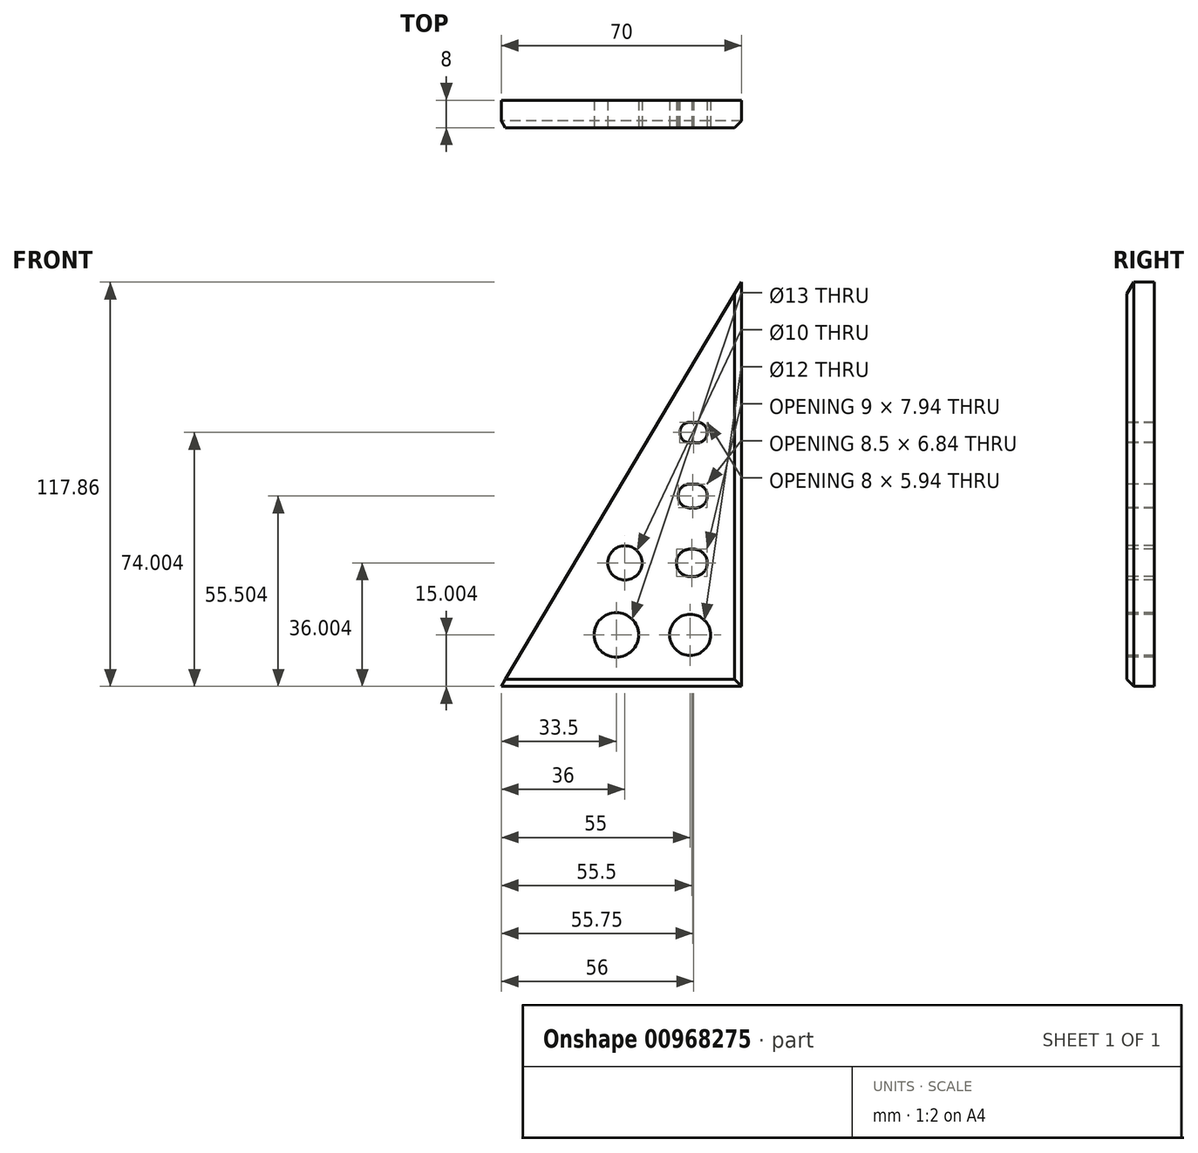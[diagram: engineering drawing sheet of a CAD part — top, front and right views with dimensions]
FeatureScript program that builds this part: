
annotation { "Feature Type Name" : "Feature", "Feature Type Description" : "" }
export const myFeature = defineFeature(function(context is Context, id is Id, definition is map)
    precondition{}
    {
        {
            var Q0;
            Q0=qCreatedBy(makeId("Front.planeOp"),FACE);
            var sketch = newSketch(context, id + "F0", { "sketchPlane" : qUnion([Q0])});
            skLineSegment(sketch, "E0", {"start": v(0, -74.8) * mm, "end": v(0, 65.2) * mm});
            skLineSegment(sketch, "E1", {"start": v(0, -74.8) * mm, "end": v(-70, -74.8) * mm});
            skLineSegment(sketch, "E2", {"start": v(-70, -74.8) * mm, "end": v(0, 65.2) * mm});
            skSolve(sketch);
        }
        {
            var Q0;
            Q0=makeQuery(id+"F0.imprint","IMPRINT",FACE,{"disambiguationData":[TD([[makeQuery(id+"F0.imprint","IMPRINT",EDGE,{"derivedFrom":sQuery(id+"F0.wireOp",EDGE,"E0")}),1.0]])]});
            extrude(context, id + "F1", {"entities" : qUnion([Q0]), "depth" : 8 * mm, "offsetDistance" : 25 * mm});
        }
        {
            var Q0;
            Q0=makeQuery(id+"F1.opExtrude","CAP_FACE",FACE,{"disambiguationData":[OSD([sQuery(id+"F0.wireOp",EDGE,"E0"),sQuery(id+"F0.wireOp",EDGE,"E1"),sQuery(id+"F0.wireOp",EDGE,"E2")])],"isStart":false});
            var sketch = newSketch(context, id + "F2", { "sketchPlane" : qUnion([Q0])});
            skLineSegment(sketch, "E3", {"start": v(0, -74.8) * mm, "end": v(-15, -74.8) * mm});
            skLineSegment(sketch, "E4", {"start": v(-15, -74.8) * mm, "end": v(-15, -64.8) * mm});
            skLineSegment(sketch, "E5", {"start": v(-15, -64.8) * mm, "end": v(-15, -58.3) * mm});
            skCircle(sketch, "E6", {"center": v(-15, -58.3) * mm, "radius": 6.5 * mm});
            skLineSegment(sketch, "E7", {"start": v(-15, -58.3) * mm, "end": v(-15, -33.8) * mm});
            skCircle(sketch, "E8", {"center": v(-15, -33.8) * mm, "radius": 6 * mm});
            skLineSegment(sketch, "E9", {"start": v(-15, -33.8) * mm, "end": v(-15, -10.8) * mm});
            skCircle(sketch, "E10", {"center": v(-15, -10.8) * mm, "radius": 5 * mm});
            skLineSegment(sketch, "E11", {"start": v(-15, -10.8) * mm, "end": v(-15, 10.2) * mm});
            skCircle(sketch, "E12", {"center": v(-15, 10.2) * mm, "radius": 4 * mm});
            skLineSegment(sketch, "E13", {"start": v(0, 65.2) * mm, "end": v(0, 115.2) * mm});
            skLineSegment(sketch, "E14", {"start": v(0, 115.2) * mm, "end": v(-70, -74.8) * mm});
            skSolve(sketch);
        }
        {
            var Q0;
            Q0=makeQuery(id+"F2.imprint","IMPRINT",FACE,{"disambiguationData":[TD([[makeQuery(id+"F2.imprint","IMPRINT",EDGE,{"derivedFrom":sQuery(id+"F2.wireOp",EDGE,"E13")}),1.0]])]});
            extrude(context, id + "F3", {"entities" : qUnion([Q0]), "operationType" : NewBodyOperationType.ADD, "oppositeDirection" : true, "depth" : 8 * mm, "offsetDistance" : 25 * mm});
        }
        {
            var Q0;
            {var subQ0=sQuery(id+"F0.wireOp",EDGE,"E2");Q0=makeQuery(id+"F3.boolean.opBoolean","MERGE",FACE,{"derivedFrom":[makeQuery(id+"F1.opExtrude","CAP_FACE",FACE,{"disambiguationData":[OSD([sQuery(id+"F0.wireOp",EDGE,"E0"),sQuery(id+"F0.wireOp",EDGE,"E1"),subQ0])],"isStart":false}),makeQuery(id+"F3.opExtrude","CAP_FACE",FACE,{"disambiguationData":[OSD([subQ0,sQuery(id+"F2.wireOp",EDGE,"E13"),sQuery(id+"F2.wireOp",EDGE,"E14")])],"isStart":true})]});}
            var sketch = newSketch(context, id + "F4", { "sketchPlane" : qUnion([Q0])});
            skLineSegment(sketch, "E15", {"start": v(0, 115.2) * mm, "end": v(0, 65.2) * mm});
            skLineSegment(sketch, "E16", {"start": v(0, 65.2) * mm, "end": v(-70, -74.8) * mm});
            skLineSegment(sketch, "E17", {"start": v(-70, -74.8) * mm, "end": v(0, 115.2) * mm});
            skSolve(sketch);
        }
        {
            var Q0;
            Q0=makeQuery(id+"F4.imprint","IMPRINT",FACE,{"disambiguationData":[TD([[makeQuery(id+"F4.imprint","IMPRINT",EDGE,{"derivedFrom":sQuery(id+"F4.wireOp",EDGE,"E15")}),1.0]])]});
            extrude(context, id + "F5", {"entities" : qUnion([Q0]), "operationType" : NewBodyOperationType.REMOVE, "oppositeDirection" : true, "depth" : 25 * mm, "offsetDistance" : 25 * mm});
        }
        {
            var Q0;
            {var subQ0=sQuery(id+"F0.wireOp",EDGE,"E2");Q0=makeQuery(id+"F3.boolean.opBoolean","MERGE",FACE,{"derivedFrom":[makeQuery(id+"F1.opExtrude","CAP_FACE",FACE,{"disambiguationData":[OSD([sQuery(id+"F0.wireOp",EDGE,"E0"),sQuery(id+"F0.wireOp",EDGE,"E1"),subQ0])],"isStart":false}),makeQuery(id+"F3.opExtrude","CAP_FACE",FACE,{"disambiguationData":[OSD([subQ0,sQuery(id+"F2.wireOp",EDGE,"E13"),sQuery(id+"F2.wireOp",EDGE,"E14")])],"isStart":true})]});}
            var sketch = newSketch(context, id + "F6", { "sketchPlane" : qUnion([Q0])});
            skLineSegment(sketch, "E18", {"start": v(0, -74.8) * mm, "end": v(-10, -74.8) * mm});
            skLineSegment(sketch, "E19", {"start": v(-10, -74.8) * mm, "end": v(-10, -64.8) * mm});
            skLineSegment(sketch, "E20", {"start": v(-10, -64.8) * mm, "end": v(-10, -59.8) * mm});
            skCircle(sketch, "E21", {"center": v(-10, -59.8) * mm, "radius": 5 * mm});
            skLineSegment(sketch, "E22", {"start": v(-10, -59.8) * mm, "end": v(-10, -38.8) * mm});
            skCircle(sketch, "E23", {"center": v(-10, -38.8) * mm, "radius": 4 * mm});
            skLineSegment(sketch, "E24", {"start": v(-10, -38.8) * mm, "end": v(-10, -19.3) * mm});
            skCircle(sketch, "E25", {"center": v(-10, -19.3) * mm, "radius": 3.5 * mm});
            skLineSegment(sketch, "E26", {"start": v(-10, -19.3) * mm, "end": v(-10, -0.8) * mm});
            skCircle(sketch, "E27", {"center": v(-10, -0.8) * mm, "radius": 3 * mm});
            skSolve(sketch);
        }
        {
            var Q0;
            {var subQ0=sQuery(id+"F6.wireOp",EDGE,"E20");Q0=makeQuery(id+"F6.imprint","IMPRINT",FACE,{"disambiguationData":[TD([[makeQuery(id+"F6.imprint","IMPRINT",EDGE,{"derivedFrom":subQ0}),-1.0]])]});}
            var Q1;
            {var subQ0=sQuery(id+"F6.wireOp",EDGE,"E20");Q1=makeQuery(id+"F6.imprint","IMPRINT",FACE,{"disambiguationData":[TD([[makeQuery(id+"F6.imprint","IMPRINT",EDGE,{"derivedFrom":subQ0}),1.0]])]});}
            var Q2;
            {var subQ0=sQuery(id+"F6.wireOp",EDGE,"E24");var subQ1=sQuery(id+"F6.wireOp",EDGE,"E22");var subQ2=makeQuery(id+"F6.imprint","INTERSECT",VERTEX,{"derivedFrom":[subQ1,subQ0]});Q2=makeQuery(id+"F6.imprint","IMPRINT",FACE,{"disambiguationData":[TD([[makeQuery(id+"F6.imprint","IMPRINT",EDGE,{"disambiguationData":[TD([[subQ2,1.0]])],"derivedFrom":subQ1}),-1.0]])]});}
            var Q3;
            {var subQ0=sQuery(id+"F6.wireOp",EDGE,"E24");var subQ1=sQuery(id+"F6.wireOp",EDGE,"E22");var subQ2=makeQuery(id+"F6.imprint","INTERSECT",VERTEX,{"derivedFrom":[subQ1,subQ0]});Q3=makeQuery(id+"F6.imprint","IMPRINT",FACE,{"disambiguationData":[TD([[makeQuery(id+"F6.imprint","IMPRINT",EDGE,{"disambiguationData":[TD([[subQ2,1.0]])],"derivedFrom":subQ1}),1.0]])]});}
            var Q4;
            {var subQ0=sQuery(id+"F6.wireOp",EDGE,"E26");var subQ1=sQuery(id+"F6.wireOp",EDGE,"E24");var subQ2=makeQuery(id+"F6.imprint","INTERSECT",VERTEX,{"derivedFrom":[subQ1,subQ0]});Q4=makeQuery(id+"F6.imprint","IMPRINT",FACE,{"disambiguationData":[TD([[makeQuery(id+"F6.imprint","IMPRINT",EDGE,{"disambiguationData":[TD([[subQ2,1.0]])],"derivedFrom":subQ1}),-1.0]])]});}
            var Q5;
            {var subQ0=sQuery(id+"F6.wireOp",EDGE,"E26");var subQ1=sQuery(id+"F6.wireOp",EDGE,"E24");var subQ2=makeQuery(id+"F6.imprint","INTERSECT",VERTEX,{"derivedFrom":[subQ1,subQ0]});Q5=makeQuery(id+"F6.imprint","IMPRINT",FACE,{"disambiguationData":[TD([[makeQuery(id+"F6.imprint","IMPRINT",EDGE,{"disambiguationData":[TD([[subQ2,1.0]])],"derivedFrom":subQ1}),1.0]])]});}
            var Q6;
            Q6=makeQuery(id+"F6.imprint","IMPRINT",FACE,{"disambiguationData":[TD([[makeQuery(id+"F6.imprint","IMPRINT",EDGE,{"derivedFrom":sQuery(id+"F6.wireOp",EDGE,"E27")}),1.0]])]});
            extrude(context, id + "F7", {"entities" : qUnion([Q0, Q1, Q2, Q3, Q4, Q5, Q6]), "operationType" : NewBodyOperationType.REMOVE, "oppositeDirection" : true, "depth" : 25 * mm, "offsetDistance" : 25 * mm});
        }
        {
            var Q0;
            {var subQ0=sQuery(id+"F0.wireOp",EDGE,"E2");Q0=makeQuery(id+"F3.boolean.opBoolean","MERGE",FACE,{"derivedFrom":[makeQuery(id+"F1.opExtrude","CAP_FACE",FACE,{"disambiguationData":[OSD([sQuery(id+"F0.wireOp",EDGE,"E0"),sQuery(id+"F0.wireOp",EDGE,"E1"),subQ0])],"isStart":false}),makeQuery(id+"F3.opExtrude","CAP_FACE",FACE,{"disambiguationData":[OSD([subQ0,sQuery(id+"F2.wireOp",EDGE,"E13"),sQuery(id+"F2.wireOp",EDGE,"E14")])],"isStart":true})]});}
            var sketch = newSketch(context, id + "F8", { "sketchPlane" : qUnion([Q0])});
            skLineSegment(sketch, "E28", {"start": v(0, 65.2) * mm, "end": v(0, 35.2) * mm});
            skLineSegment(sketch, "E29", {"start": v(0, 35.2) * mm, "end": v(-70, -74.8) * mm});
            skLineSegment(sketch, "E30", {"start": v(-70, -74.8) * mm, "end": v(0, 65.2) * mm});
            skSolve(sketch);
        }
        {
            var Q0;
            Q0=makeQuery(id+"F8.imprint","IMPRINT",FACE,{"disambiguationData":[TD([[makeQuery(id+"F8.imprint","IMPRINT",EDGE,{"derivedFrom":sQuery(id+"F8.wireOp",EDGE,"E28")}),1.0]])]});
            extrude(context, id + "F9", {"entities" : qUnion([Q0]), "operationType" : NewBodyOperationType.REMOVE, "oppositeDirection" : true, "depth" : 25 * mm, "offsetDistance" : 25 * mm});
        }
        {
            var Q0;
            {var subQ0=sQuery(id+"F0.wireOp",EDGE,"E2");Q0=makeQuery(id+"F3.boolean.opBoolean","MERGE",FACE,{"derivedFrom":[makeQuery(id+"F1.opExtrude","CAP_FACE",FACE,{"disambiguationData":[OSD([sQuery(id+"F0.wireOp",EDGE,"E0"),sQuery(id+"F0.wireOp",EDGE,"E1"),subQ0])],"isStart":false}),makeQuery(id+"F3.opExtrude","CAP_FACE",FACE,{"disambiguationData":[OSD([subQ0,sQuery(id+"F2.wireOp",EDGE,"E13"),sQuery(id+"F2.wireOp",EDGE,"E14")])],"isStart":true})]});}
            var sketch = newSketch(context, id + "F10", { "sketchPlane" : qUnion([Q0])});
            skLineSegment(sketch, "E31", {"start": v(0, 35.2) * mm, "end": v(8.94, 49.24) * mm});
            skLineSegment(sketch, "E32", {"start": v(0, -74.8) * mm, "end": v(5, -74.8) * mm});
            skLineSegment(sketch, "E33", {"start": v(5, -74.8) * mm, "end": v(5, 43.05) * mm});
            skSolve(sketch);
        }
        {
            var Q0;
            Q0=makeQuery(id+"F10.imprint","IMPRINT",FACE,{"disambiguationData":[TD([[makeQuery(id+"F10.imprint","IMPRINT",EDGE,{"derivedFrom":sQuery(id+"F10.wireOp",EDGE,"E32")}),1.0]])]});
            extrude(context, id + "F11", {"entities" : qUnion([Q0]), "operationType" : NewBodyOperationType.ADD, "oppositeDirection" : true, "depth" : 8 * mm, "offsetDistance" : 25 * mm});
        }
        {
            var Q0;
            {var subQ0=sQuery(id+"F2.wireOp",EDGE,"E13");var subQ1=sQuery(id+"F0.wireOp",EDGE,"E0");var subQ2=sQuery(id+"F0.wireOp",EDGE,"E2");Q0=makeQuery(id+"F11.boolean.opBoolean","MERGE",FACE,{"derivedFrom":[makeQuery(id+"F3.boolean.opBoolean","MERGE",FACE,{"derivedFrom":[makeQuery(id+"F1.opExtrude","CAP_FACE",FACE,{"disambiguationData":[OSD([subQ1,sQuery(id+"F0.wireOp",EDGE,"E1"),subQ2])],"isStart":false}),makeQuery(id+"F3.opExtrude","CAP_FACE",FACE,{"disambiguationData":[OSD([subQ2,subQ0,sQuery(id+"F2.wireOp",EDGE,"E14")])],"isStart":true})]}),makeQuery(id+"F11.opExtrude","CAP_FACE",FACE,{"disambiguationData":[OSD([subQ1,subQ0,sQuery(id+"F10.wireOp",EDGE,"E31"),sQuery(id+"F10.wireOp",EDGE,"E32"),sQuery(id+"F10.wireOp",EDGE,"E33")])],"isStart":true})]});}
            var sketch = newSketch(context, id + "F12", { "sketchPlane" : qUnion([Q0])});
            skLineSegment(sketch, "E34", {"start": v(-70, -74.8) * mm, "end": v(-65, -74.8) * mm});
            skLineSegment(sketch, "E35", {"start": v(-65, -74.8) * mm, "end": v(5, 43.05) * mm});
            skLineSegment(sketch, "E36", {"start": v(5, 43.05) * mm, "end": v(-70, -74.8) * mm});
            skSolve(sketch);
        }
        {
            var Q0;
            Q0=makeQuery(id+"F12.imprint","IMPRINT",FACE,{"disambiguationData":[TD([[makeQuery(id+"F12.imprint","IMPRINT",EDGE,{"derivedFrom":sQuery(id+"F12.wireOp",EDGE,"E34")}),-1.0]])]});
            extrude(context, id + "F13", {"entities" : qUnion([Q0]), "operationType" : NewBodyOperationType.REMOVE, "oppositeDirection" : true, "depth" : 25 * mm, "offsetDistance" : 25 * mm});
        }
        {
            var Q0;
            {var subQ0=sQuery(id+"F2.wireOp",EDGE,"E13");var subQ1=sQuery(id+"F0.wireOp",EDGE,"E0");var subQ2=sQuery(id+"F0.wireOp",EDGE,"E2");Q0=makeQuery(id+"F11.boolean.opBoolean","MERGE",FACE,{"derivedFrom":[makeQuery(id+"F3.boolean.opBoolean","MERGE",FACE,{"derivedFrom":[makeQuery(id+"F1.opExtrude","CAP_FACE",FACE,{"disambiguationData":[OSD([subQ1,sQuery(id+"F0.wireOp",EDGE,"E1"),subQ2])],"isStart":false}),makeQuery(id+"F3.opExtrude","CAP_FACE",FACE,{"disambiguationData":[OSD([subQ2,subQ0,sQuery(id+"F2.wireOp",EDGE,"E14")])],"isStart":true})]}),makeQuery(id+"F11.opExtrude","CAP_FACE",FACE,{"disambiguationData":[OSD([subQ1,subQ0,sQuery(id+"F10.wireOp",EDGE,"E31"),sQuery(id+"F10.wireOp",EDGE,"E32"),sQuery(id+"F10.wireOp",EDGE,"E33")])],"isStart":true})]});}
            var sketch = newSketch(context, id + "F14", { "sketchPlane" : qUnion([Q0])});
            skCircle(sketch, "E37", {"center": v(-10, -38.8) * mm, "radius": 6.34 * mm});
            skCircle(sketch, "E38", {"center": v(-10, -19.3) * mm, "radius": 6.83 * mm});
            skCircle(sketch, "E39", {"center": v(-10, -0.8) * mm, "radius": 5.3 * mm});
            skSolve(sketch);
        }
        {
            var Q0;
            Q0=makeQuery(id+"F14.imprint","IMPRINT",FACE,{"disambiguationData":[TD([[makeQuery(id+"F14.imprint","IMPRINT",EDGE,{"derivedFrom":sQuery(id+"F14.wireOp",EDGE,"E37")}),1.0]])]});
            var Q1;
            Q1=makeQuery(id+"F14.imprint","IMPRINT",FACE,{"disambiguationData":[TD([[makeQuery(id+"F14.imprint","IMPRINT",EDGE,{"derivedFrom":makeQuery(id+"F7.boolean.opBoolean","COPY",EDGE,{"derivedFrom":makeQuery(id+"F7.opExtrude","CAP_EDGE",EDGE,{"disambiguationData":[OSD([sQuery(id+"F6.wireOp",EDGE,"E23")])],"isStart":true})})}),1.0]])]});
            var Q2;
            Q2=makeQuery(id+"F14.imprint","IMPRINT",FACE,{"disambiguationData":[TD([[makeQuery(id+"F14.imprint","IMPRINT",EDGE,{"derivedFrom":sQuery(id+"F14.wireOp",EDGE,"E38")}),1.0]])]});
            var Q3;
            Q3=makeQuery(id+"F14.imprint","IMPRINT",FACE,{"disambiguationData":[TD([[makeQuery(id+"F14.imprint","IMPRINT",EDGE,{"derivedFrom":makeQuery(id+"F7.boolean.opBoolean","COPY",EDGE,{"derivedFrom":makeQuery(id+"F7.opExtrude","CAP_EDGE",EDGE,{"disambiguationData":[OSD([sQuery(id+"F6.wireOp",EDGE,"E25")])],"isStart":true})})}),1.0]])]});
            var Q4;
            Q4=makeQuery(id+"F14.imprint","IMPRINT",FACE,{"disambiguationData":[TD([[makeQuery(id+"F14.imprint","IMPRINT",EDGE,{"derivedFrom":sQuery(id+"F14.wireOp",EDGE,"E39")}),1.0]])]});
            var Q5;
            Q5=makeQuery(id+"F14.imprint","IMPRINT",FACE,{"disambiguationData":[TD([[makeQuery(id+"F14.imprint","IMPRINT",EDGE,{"derivedFrom":makeQuery(id+"F7.boolean.opBoolean","COPY",EDGE,{"derivedFrom":makeQuery(id+"F7.opExtrude","CAP_EDGE",EDGE,{"disambiguationData":[OSD([sQuery(id+"F6.wireOp",EDGE,"E27")])],"isStart":true})})}),1.0]])]});
            extrude(context, id + "F15", {"entities" : qUnion([Q0, Q1, Q2, Q3, Q4, Q5]), "operationType" : NewBodyOperationType.ADD, "oppositeDirection" : true, "depth" : 8 * mm, "offsetDistance" : 25 * mm});
        }
        {
            var Q0;
            {var subQ0=sQuery(id+"F2.wireOp",EDGE,"E13");var subQ1=sQuery(id+"F0.wireOp",EDGE,"E0");var subQ2=sQuery(id+"F0.wireOp",EDGE,"E2");Q0=makeQuery(id+"F15.boolean.opBoolean","MERGE",FACE,{"derivedFrom":[makeQuery(id+"F11.boolean.opBoolean","MERGE",FACE,{"derivedFrom":[makeQuery(id+"F3.boolean.opBoolean","MERGE",FACE,{"derivedFrom":[makeQuery(id+"F1.opExtrude","CAP_FACE",FACE,{"disambiguationData":[OSD([subQ1,sQuery(id+"F0.wireOp",EDGE,"E1"),subQ2])],"isStart":false}),makeQuery(id+"F3.opExtrude","CAP_FACE",FACE,{"disambiguationData":[OSD([subQ2,subQ0,sQuery(id+"F2.wireOp",EDGE,"E14")])],"isStart":true})]}),makeQuery(id+"F11.opExtrude","CAP_FACE",FACE,{"disambiguationData":[OSD([subQ1,subQ0,sQuery(id+"F10.wireOp",EDGE,"E31"),sQuery(id+"F10.wireOp",EDGE,"E32"),sQuery(id+"F10.wireOp",EDGE,"E33")])],"isStart":true})]}),makeQuery(id+"F15.opExtrude","CAP_FACE",FACE,{"disambiguationData":[OSD([sQuery(id+"F14.wireOp",EDGE,"E37")])],"isStart":true}),makeQuery(id+"F15.opExtrude","CAP_FACE",FACE,{"disambiguationData":[OSD([sQuery(id+"F14.wireOp",EDGE,"E38")])],"isStart":true}),makeQuery(id+"F15.opExtrude","CAP_FACE",FACE,{"disambiguationData":[OSD([sQuery(id+"F14.wireOp",EDGE,"E39")])],"isStart":true})]});}
            var sketch = newSketch(context, id + "F16", { "sketchPlane" : qUnion([Q0])});
            skLineSegment(sketch, "E40", {"start": v(-10, -59.8) * mm, "end": v(-5, -59.8) * mm});
            skLineSegment(sketch, "E41", {"start": v(-5, -59.8) * mm, "end": v(-5, 40.97) * mm});
            skLineSegment(sketch, "E42", {"start": v(-5, -59.8) * mm, "end": v(-5, -38.8) * mm});
            skLineSegment(sketch, "E43", {"start": v(-5, -38.8) * mm, "end": v(-9, -38.8) * mm});
            skCircle(sketch, "E44", {"center": v(-9, -38.8) * mm, "radius": 4 * mm});
            skLineSegment(sketch, "E45", {"start": v(-5, -38.8) * mm, "end": v(-5, -19.3) * mm});
            skLineSegment(sketch, "E46", {"start": v(-5, -19.3) * mm, "end": v(-8.5, -19.3) * mm});
            skCircle(sketch, "E47", {"center": v(-8.5, -19.3) * mm, "radius": 3.5 * mm});
            skLineSegment(sketch, "E48", {"start": v(-5, -19.3) * mm, "end": v(-5, -0.8) * mm});
            skLineSegment(sketch, "E49", {"start": v(-5, -0.8) * mm, "end": v(-8, -0.8) * mm});
            skCircle(sketch, "E50", {"center": v(-8, -0.8) * mm, "radius": 3 * mm});
            skSolve(sketch);
        }
        {
            var Q0;
            Q0=makeQuery(id+"F16.imprint","IMPRINT",FACE,{"disambiguationData":[TD([[makeQuery(id+"F16.imprint","IMPRINT",EDGE,{"derivedFrom":sQuery(id+"F16.wireOp",EDGE,"E44")}),1.0]])]});
            var Q1;
            Q1=makeQuery(id+"F16.imprint","IMPRINT",FACE,{"disambiguationData":[TD([[makeQuery(id+"F16.imprint","IMPRINT",EDGE,{"derivedFrom":sQuery(id+"F16.wireOp",EDGE,"E47")}),1.0]])]});
            var Q2;
            Q2=makeQuery(id+"F16.imprint","IMPRINT",FACE,{"disambiguationData":[TD([[makeQuery(id+"F16.imprint","IMPRINT",EDGE,{"derivedFrom":sQuery(id+"F16.wireOp",EDGE,"E50")}),1.0]])]});
            extrude(context, id + "F17", {"entities" : qUnion([Q0, Q1, Q2]), "operationType" : NewBodyOperationType.REMOVE, "oppositeDirection" : true, "depth" : 25 * mm, "offsetDistance" : 25 * mm});
        }
        {
            var Q0;
            {var subQ0=sQuery(id+"F2.wireOp",EDGE,"E13");var subQ1=sQuery(id+"F0.wireOp",EDGE,"E0");var subQ2=sQuery(id+"F0.wireOp",EDGE,"E2");Q0=makeQuery(id+"F15.boolean.opBoolean","MERGE",FACE,{"derivedFrom":[makeQuery(id+"F11.boolean.opBoolean","MERGE",FACE,{"derivedFrom":[makeQuery(id+"F3.boolean.opBoolean","MERGE",FACE,{"derivedFrom":[makeQuery(id+"F1.opExtrude","CAP_FACE",FACE,{"disambiguationData":[OSD([subQ1,sQuery(id+"F0.wireOp",EDGE,"E1"),subQ2])],"isStart":false}),makeQuery(id+"F3.opExtrude","CAP_FACE",FACE,{"disambiguationData":[OSD([subQ2,subQ0,sQuery(id+"F2.wireOp",EDGE,"E14")])],"isStart":true})]}),makeQuery(id+"F11.opExtrude","CAP_FACE",FACE,{"disambiguationData":[OSD([subQ1,subQ0,sQuery(id+"F10.wireOp",EDGE,"E31"),sQuery(id+"F10.wireOp",EDGE,"E32"),sQuery(id+"F10.wireOp",EDGE,"E33")])],"isStart":true})]}),makeQuery(id+"F15.opExtrude","CAP_FACE",FACE,{"disambiguationData":[OSD([sQuery(id+"F14.wireOp",EDGE,"E37")])],"isStart":true}),makeQuery(id+"F15.opExtrude","CAP_FACE",FACE,{"disambiguationData":[OSD([sQuery(id+"F14.wireOp",EDGE,"E38")])],"isStart":true}),makeQuery(id+"F15.opExtrude","CAP_FACE",FACE,{"disambiguationData":[OSD([sQuery(id+"F14.wireOp",EDGE,"E39")])],"isStart":true})]});}
            var sketch = newSketch(context, id + "F18", { "sketchPlane" : qUnion([Q0])});
            skLineSegment(sketch, "E51", {"start": v(-10, -59.8) * mm, "end": v(-31.5, -59.8) * mm});
            skCircle(sketch, "E52", {"center": v(-31.5, -59.8) * mm, "radius": 6.5 * mm});
            skLineSegment(sketch, "E53", {"start": v(-9, -38.8) * mm, "end": v(-29, -38.8) * mm});
            skCircle(sketch, "E54", {"center": v(-29, -38.8) * mm, "radius": 6 * mm});
            skSolve(sketch);
        }
        {
            var Q0;
            Q0=makeQuery(id+"F18.imprint","IMPRINT",FACE,{"disambiguationData":[TD([[makeQuery(id+"F18.imprint","IMPRINT",EDGE,{"derivedFrom":sQuery(id+"F18.wireOp",EDGE,"E52")}),1.0]])]});
            var Q1;
            Q1=makeQuery(id+"F18.imprint","IMPRINT",FACE,{"disambiguationData":[TD([[makeQuery(id+"F18.imprint","IMPRINT",EDGE,{"derivedFrom":sQuery(id+"F18.wireOp",EDGE,"E54")}),1.0]])]});
            extrude(context, id + "F19", {"entities" : qUnion([Q0, Q1]), "operationType" : NewBodyOperationType.REMOVE, "oppositeDirection" : true, "depth" : 25 * mm, "offsetDistance" : 25 * mm});
        }
        {
            var Q0;
            {var subQ0=sQuery(id+"F2.wireOp",EDGE,"E13");var subQ1=sQuery(id+"F0.wireOp",EDGE,"E0");var subQ2=sQuery(id+"F0.wireOp",EDGE,"E2");Q0=makeQuery(id+"F15.boolean.opBoolean","MERGE",FACE,{"derivedFrom":[makeQuery(id+"F11.boolean.opBoolean","MERGE",FACE,{"derivedFrom":[makeQuery(id+"F3.boolean.opBoolean","MERGE",FACE,{"derivedFrom":[makeQuery(id+"F1.opExtrude","CAP_FACE",FACE,{"disambiguationData":[OSD([subQ1,sQuery(id+"F0.wireOp",EDGE,"E1"),subQ2])],"isStart":false}),makeQuery(id+"F3.opExtrude","CAP_FACE",FACE,{"disambiguationData":[OSD([subQ2,subQ0,sQuery(id+"F2.wireOp",EDGE,"E14")])],"isStart":true})]}),makeQuery(id+"F11.opExtrude","CAP_FACE",FACE,{"disambiguationData":[OSD([subQ1,subQ0,sQuery(id+"F10.wireOp",EDGE,"E31"),sQuery(id+"F10.wireOp",EDGE,"E32"),sQuery(id+"F10.wireOp",EDGE,"E33")])],"isStart":true})]}),makeQuery(id+"F15.opExtrude","CAP_FACE",FACE,{"disambiguationData":[OSD([sQuery(id+"F14.wireOp",EDGE,"E37")])],"isStart":true}),makeQuery(id+"F15.opExtrude","CAP_FACE",FACE,{"disambiguationData":[OSD([sQuery(id+"F14.wireOp",EDGE,"E38")])],"isStart":true}),makeQuery(id+"F15.opExtrude","CAP_FACE",FACE,{"disambiguationData":[OSD([sQuery(id+"F14.wireOp",EDGE,"E39")])],"isStart":true})]});}
            var sketch = newSketch(context, id + "F20", { "sketchPlane" : qUnion([Q0])});
            skCircle(sketch, "E55", {"center": v(-10, -59.8) * mm, "radius": 6.5 * mm});
            skSolve(sketch);
        }
        {
            var Q0;
            Q0=makeQuery(id+"F20.imprint","IMPRINT",FACE,{"disambiguationData":[TD([[makeQuery(id+"F20.imprint","IMPRINT",EDGE,{"derivedFrom":sQuery(id+"F20.wireOp",EDGE,"E55")}),1.0]])]});
            extrude(context, id + "F21", {"entities" : qUnion([Q0]), "operationType" : NewBodyOperationType.REMOVE, "oppositeDirection" : true, "depth" : 25 * mm, "offsetDistance" : 25 * mm});
        }
        {
            var Q0;
            {var subQ0=sQuery(id+"F2.wireOp",EDGE,"E13");var subQ1=sQuery(id+"F0.wireOp",EDGE,"E0");var subQ2=sQuery(id+"F0.wireOp",EDGE,"E2");Q0=makeQuery(id+"F15.boolean.opBoolean","MERGE",FACE,{"derivedFrom":[makeQuery(id+"F11.boolean.opBoolean","MERGE",FACE,{"derivedFrom":[makeQuery(id+"F3.boolean.opBoolean","MERGE",FACE,{"derivedFrom":[makeQuery(id+"F1.opExtrude","CAP_FACE",FACE,{"disambiguationData":[OSD([subQ1,sQuery(id+"F0.wireOp",EDGE,"E1"),subQ2])],"isStart":false}),makeQuery(id+"F3.opExtrude","CAP_FACE",FACE,{"disambiguationData":[OSD([subQ2,subQ0,sQuery(id+"F2.wireOp",EDGE,"E14")])],"isStart":true})]}),makeQuery(id+"F11.opExtrude","CAP_FACE",FACE,{"disambiguationData":[OSD([subQ1,subQ0,sQuery(id+"F10.wireOp",EDGE,"E31"),sQuery(id+"F10.wireOp",EDGE,"E32"),sQuery(id+"F10.wireOp",EDGE,"E33")])],"isStart":true})]}),makeQuery(id+"F15.opExtrude","CAP_FACE",FACE,{"disambiguationData":[OSD([sQuery(id+"F14.wireOp",EDGE,"E37")])],"isStart":true}),makeQuery(id+"F15.opExtrude","CAP_FACE",FACE,{"disambiguationData":[OSD([sQuery(id+"F14.wireOp",EDGE,"E38")])],"isStart":true}),makeQuery(id+"F15.opExtrude","CAP_FACE",FACE,{"disambiguationData":[OSD([sQuery(id+"F14.wireOp",EDGE,"E39")])],"isStart":true})]});}
            var sketch = newSketch(context, id + "F22", { "sketchPlane" : qUnion([Q0])});
            skCircle(sketch, "E56", {"center": v(-29, -38.8) * mm, "radius": 5 * mm});
            skSolve(sketch);
        }
        {
            var Q0;
            Q0=makeQuery(id+"F22.imprint","IMPRINT",FACE,{"disambiguationData":[TD([[makeQuery(id+"F22.imprint","IMPRINT",EDGE,{"derivedFrom":sQuery(id+"F22.wireOp",EDGE,"E56")}),-1.0]])]});
            extrude(context, id + "F23", {"entities" : qUnion([Q0]), "operationType" : NewBodyOperationType.ADD, "oppositeDirection" : true, "depth" : 8 * mm, "offsetDistance" : 25 * mm});
        }
        {
            var Q0;
            {var subQ0=sQuery(id+"F2.wireOp",EDGE,"E13");var subQ1=sQuery(id+"F0.wireOp",EDGE,"E0");var subQ2=sQuery(id+"F0.wireOp",EDGE,"E2");Q0=makeQuery(id+"F23.boolean.opBoolean","MERGE",FACE,{"derivedFrom":[makeQuery(id+"F15.boolean.opBoolean","MERGE",FACE,{"derivedFrom":[makeQuery(id+"F11.boolean.opBoolean","MERGE",FACE,{"derivedFrom":[makeQuery(id+"F3.boolean.opBoolean","MERGE",FACE,{"derivedFrom":[makeQuery(id+"F1.opExtrude","CAP_FACE",FACE,{"disambiguationData":[OSD([subQ1,sQuery(id+"F0.wireOp",EDGE,"E1"),subQ2])],"isStart":false}),makeQuery(id+"F3.opExtrude","CAP_FACE",FACE,{"disambiguationData":[OSD([subQ2,subQ0,sQuery(id+"F2.wireOp",EDGE,"E14")])],"isStart":true})]}),makeQuery(id+"F11.opExtrude","CAP_FACE",FACE,{"disambiguationData":[OSD([subQ1,subQ0,sQuery(id+"F10.wireOp",EDGE,"E31"),sQuery(id+"F10.wireOp",EDGE,"E32"),sQuery(id+"F10.wireOp",EDGE,"E33")])],"isStart":true})]}),makeQuery(id+"F15.opExtrude","CAP_FACE",FACE,{"disambiguationData":[OSD([sQuery(id+"F14.wireOp",EDGE,"E37")])],"isStart":true}),makeQuery(id+"F15.opExtrude","CAP_FACE",FACE,{"disambiguationData":[OSD([sQuery(id+"F14.wireOp",EDGE,"E38")])],"isStart":true}),makeQuery(id+"F15.opExtrude","CAP_FACE",FACE,{"disambiguationData":[OSD([sQuery(id+"F14.wireOp",EDGE,"E39")])],"isStart":true})]}),makeQuery(id+"F23.opExtrude","CAP_FACE",FACE,{"disambiguationData":[OSD([sQuery(id+"F18.wireOp",EDGE,"E54"),sQuery(id+"F22.wireOp",EDGE,"E56")])],"isStart":true})]});}
            var sketch = newSketch(context, id + "F24", { "sketchPlane" : qUnion([Q0])});
            skCircle(sketch, "E57", {"center": v(-31.5, -59.8) * mm, "radius": 9.68 * mm});
            skSolve(sketch);
        }
        {
            var Q0;
            Q0=makeQuery(id+"F24.imprint","IMPRINT",FACE,{"disambiguationData":[TD([[makeQuery(id+"F24.imprint","IMPRINT",EDGE,{"derivedFrom":makeQuery(id+"F19.boolean.opBoolean","COPY",EDGE,{"derivedFrom":makeQuery(id+"F19.opExtrude","CAP_EDGE",EDGE,{"disambiguationData":[OSD([sQuery(id+"F18.wireOp",EDGE,"E52")])],"isStart":true})})}),1.0]])]});
            var Q1;
            Q1=makeQuery(id+"F24.imprint","IMPRINT",FACE,{"disambiguationData":[TD([[makeQuery(id+"F24.imprint","IMPRINT",EDGE,{"derivedFrom":sQuery(id+"F24.wireOp",EDGE,"E57")}),1.0]])]});
            extrude(context, id + "F25", {"entities" : qUnion([Q0, Q1]), "operationType" : NewBodyOperationType.ADD, "oppositeDirection" : true, "depth" : 8 * mm, "offsetDistance" : 25 * mm});
        }
        {
            var Q0;
            {var subQ0=sQuery(id+"F2.wireOp",EDGE,"E13");var subQ1=sQuery(id+"F0.wireOp",EDGE,"E0");var subQ2=sQuery(id+"F0.wireOp",EDGE,"E2");Q0=makeQuery(id+"F25.boolean.opBoolean","MERGE",FACE,{"derivedFrom":[makeQuery(id+"F23.boolean.opBoolean","MERGE",FACE,{"derivedFrom":[makeQuery(id+"F15.boolean.opBoolean","MERGE",FACE,{"derivedFrom":[makeQuery(id+"F11.boolean.opBoolean","MERGE",FACE,{"derivedFrom":[makeQuery(id+"F3.boolean.opBoolean","MERGE",FACE,{"derivedFrom":[makeQuery(id+"F1.opExtrude","CAP_FACE",FACE,{"disambiguationData":[OSD([subQ1,sQuery(id+"F0.wireOp",EDGE,"E1"),subQ2])],"isStart":false}),makeQuery(id+"F3.opExtrude","CAP_FACE",FACE,{"disambiguationData":[OSD([subQ2,subQ0,sQuery(id+"F2.wireOp",EDGE,"E14")])],"isStart":true})]}),makeQuery(id+"F11.opExtrude","CAP_FACE",FACE,{"disambiguationData":[OSD([subQ1,subQ0,sQuery(id+"F10.wireOp",EDGE,"E31"),sQuery(id+"F10.wireOp",EDGE,"E32"),sQuery(id+"F10.wireOp",EDGE,"E33")])],"isStart":true})]}),makeQuery(id+"F15.opExtrude","CAP_FACE",FACE,{"disambiguationData":[OSD([sQuery(id+"F14.wireOp",EDGE,"E37")])],"isStart":true}),makeQuery(id+"F15.opExtrude","CAP_FACE",FACE,{"disambiguationData":[OSD([sQuery(id+"F14.wireOp",EDGE,"E38")])],"isStart":true}),makeQuery(id+"F15.opExtrude","CAP_FACE",FACE,{"disambiguationData":[OSD([sQuery(id+"F14.wireOp",EDGE,"E39")])],"isStart":true})]}),makeQuery(id+"F23.opExtrude","CAP_FACE",FACE,{"disambiguationData":[OSD([sQuery(id+"F18.wireOp",EDGE,"E54"),sQuery(id+"F22.wireOp",EDGE,"E56")])],"isStart":true})]}),makeQuery(id+"F25.opExtrude","CAP_FACE",FACE,{"disambiguationData":[OSD([sQuery(id+"F24.wireOp",EDGE,"E57")])],"isStart":true})]});}
            var sketch = newSketch(context, id + "F26", { "sketchPlane" : qUnion([Q0])});
            skCircle(sketch, "E58", {"center": v(-10, -59.8) * mm, "radius": 6 * mm});
            skSolve(sketch);
        }
        {
            var Q0;
            Q0=makeQuery(id+"F26.imprint","IMPRINT",FACE,{"disambiguationData":[TD([[makeQuery(id+"F26.imprint","IMPRINT",EDGE,{"derivedFrom":sQuery(id+"F26.wireOp",EDGE,"E58")}),-1.0]])]});
            extrude(context, id + "F27", {"entities" : qUnion([Q0]), "operationType" : NewBodyOperationType.ADD, "oppositeDirection" : true, "depth" : 8 * mm, "offsetDistance" : 25 * mm});
        }
        {
            var Q0;
            {var subQ0=sQuery(id+"F2.wireOp",EDGE,"E13");var subQ1=sQuery(id+"F0.wireOp",EDGE,"E0");var subQ2=sQuery(id+"F0.wireOp",EDGE,"E2");Q0=makeQuery(id+"F27.boolean.opBoolean","MERGE",FACE,{"derivedFrom":[makeQuery(id+"F25.boolean.opBoolean","MERGE",FACE,{"derivedFrom":[makeQuery(id+"F23.boolean.opBoolean","MERGE",FACE,{"derivedFrom":[makeQuery(id+"F15.boolean.opBoolean","MERGE",FACE,{"derivedFrom":[makeQuery(id+"F11.boolean.opBoolean","MERGE",FACE,{"derivedFrom":[makeQuery(id+"F3.boolean.opBoolean","MERGE",FACE,{"derivedFrom":[makeQuery(id+"F1.opExtrude","CAP_FACE",FACE,{"disambiguationData":[OSD([subQ1,sQuery(id+"F0.wireOp",EDGE,"E1"),subQ2])],"isStart":false}),makeQuery(id+"F3.opExtrude","CAP_FACE",FACE,{"disambiguationData":[OSD([subQ2,subQ0,sQuery(id+"F2.wireOp",EDGE,"E14")])],"isStart":true})]}),makeQuery(id+"F11.opExtrude","CAP_FACE",FACE,{"disambiguationData":[OSD([subQ1,subQ0,sQuery(id+"F10.wireOp",EDGE,"E31"),sQuery(id+"F10.wireOp",EDGE,"E32"),sQuery(id+"F10.wireOp",EDGE,"E33")])],"isStart":true})]}),makeQuery(id+"F15.opExtrude","CAP_FACE",FACE,{"disambiguationData":[OSD([sQuery(id+"F14.wireOp",EDGE,"E37")])],"isStart":true}),makeQuery(id+"F15.opExtrude","CAP_FACE",FACE,{"disambiguationData":[OSD([sQuery(id+"F14.wireOp",EDGE,"E38")])],"isStart":true}),makeQuery(id+"F15.opExtrude","CAP_FACE",FACE,{"disambiguationData":[OSD([sQuery(id+"F14.wireOp",EDGE,"E39")])],"isStart":true})]}),makeQuery(id+"F23.opExtrude","CAP_FACE",FACE,{"disambiguationData":[OSD([sQuery(id+"F18.wireOp",EDGE,"E54"),sQuery(id+"F22.wireOp",EDGE,"E56")])],"isStart":true})]}),makeQuery(id+"F25.opExtrude","CAP_FACE",FACE,{"disambiguationData":[OSD([sQuery(id+"F24.wireOp",EDGE,"E57")])],"isStart":true})]}),makeQuery(id+"F27.opExtrude","CAP_FACE",FACE,{"disambiguationData":[OSD([sQuery(id+"F20.wireOp",EDGE,"E55"),sQuery(id+"F26.wireOp",EDGE,"E58")])],"isStart":true})]});}
            var sketch = newSketch(context, id + "F28", { "sketchPlane" : qUnion([Q0])});
            skLineSegment(sketch, "E59", {"start": v(-10, -59.8) * mm, "end": v(-37.5, -59.8) * mm});
            skCircle(sketch, "E60", {"center": v(-37.5, -59.8) * mm, "radius": 6.5 * mm});
            skLineSegment(sketch, "E61", {"start": v(-37.5, -59.8) * mm, "end": v(-13.8, -25.68) * mm});
            skSolve(sketch);
        }
        {
            var Q0;
            {var subQ0=sQuery(id+"F28.wireOp",EDGE,"E61");var subQ1=sQuery(id+"F28.wireOp",EDGE,"E59");var subQ2=makeQuery(id+"F28.imprint","INTERSECT",VERTEX,{"derivedFrom":[subQ1,subQ0]});Q0=makeQuery(id+"F28.imprint","IMPRINT",FACE,{"disambiguationData":[TD([[makeQuery(id+"F28.imprint","IMPRINT",EDGE,{"disambiguationData":[TD([[subQ2,1.0]])],"derivedFrom":subQ1}),1.0]])]});}
            var Q1;
            {var subQ0=sQuery(id+"F28.wireOp",EDGE,"E61");var subQ1=sQuery(id+"F28.wireOp",EDGE,"E59");var subQ2=makeQuery(id+"F28.imprint","INTERSECT",VERTEX,{"derivedFrom":[subQ1,subQ0]});Q1=makeQuery(id+"F28.imprint","IMPRINT",FACE,{"disambiguationData":[TD([[makeQuery(id+"F28.imprint","IMPRINT",EDGE,{"disambiguationData":[TD([[subQ2,1.0]])],"derivedFrom":subQ1}),-1.0]])]});}
            extrude(context, id + "F29", {"entities" : qUnion([Q0, Q1]), "operationType" : NewBodyOperationType.REMOVE, "oppositeDirection" : true, "depth" : 25 * mm, "offsetDistance" : 25 * mm});
        }
        {
            var Q0;
            Q0=makeQuery(id+"F11.opExtrude","CAP_EDGE",EDGE,{"disambiguationData":[OSD([sQuery(id+"F10.wireOp",EDGE,"E33")])],"isStart":true});
            var Q1;
            Q1=makeQuery(id+"F13.boolean.opBoolean","COPY",EDGE,{"derivedFrom":makeQuery(id+"F13.opExtrude","CAP_EDGE",EDGE,{"disambiguationData":[OSD([sQuery(id+"F12.wireOp",EDGE,"E35")])],"isStart":true})});
            var Q2;
            Q2=makeQuery(id+"F11.boolean.opBoolean","MERGE",EDGE,{"derivedFrom":[makeQuery(id+"F1.opExtrude","CAP_EDGE",EDGE,{"disambiguationData":[OSD([sQuery(id+"F0.wireOp",EDGE,"E1")])],"isStart":false}),makeQuery(id+"F11.opExtrude","CAP_EDGE",EDGE,{"disambiguationData":[OSD([sQuery(id+"F10.wireOp",EDGE,"E32")])],"isStart":true})]});
            chamfer(context, id + "F30", {"entities" : qUnion([Q0, Q1, Q2]), "width" : 2 * mm, "tangentPropagation" : true});
        }
    });
